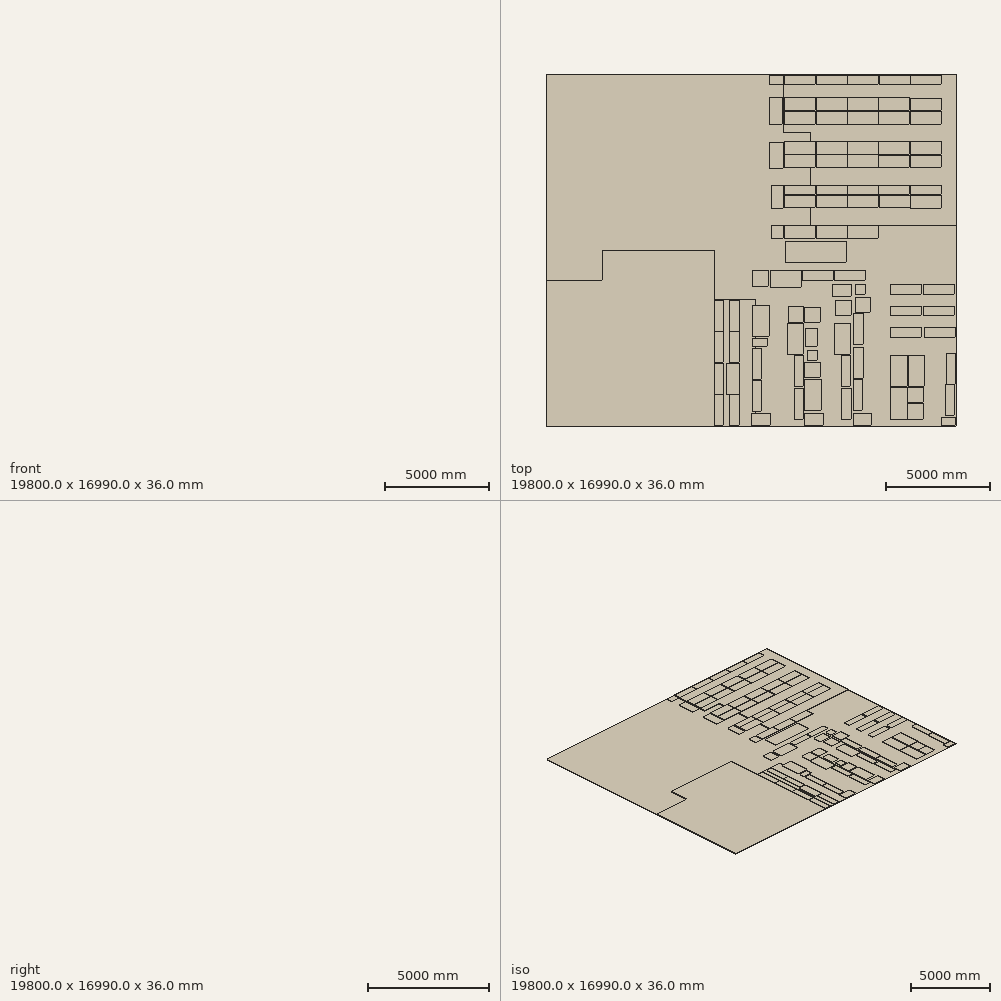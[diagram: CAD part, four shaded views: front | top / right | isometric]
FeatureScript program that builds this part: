
annotation { "Feature Type Name" : "Feature", "Feature Type Description" : "" }
export const myFeature = defineFeature(function(context is Context, id is Id, definition is map)
    precondition{}
    {
        {
            var Q0;
            Q0=qCreatedBy(makeId("Top.planeOp"),FACE);
            var sketch = newSketch(context, id + "F0", { "sketchPlane" : qUnion([Q0])});
            skLineSegment(sketch, "E0.bottom", {"start": v(9900, -8495) * mm, "end": v(-9900, -8495) * mm});
            skLineSegment(sketch, "E0.top", {"start": v(9900, 8495) * mm, "end": v(-9900, 8495) * mm});
            skLineSegment(sketch, "E0.left", {"start": v(9900, -8495) * mm, "end": v(9900, 8495) * mm});
            skLineSegment(sketch, "E0.right", {"start": v(-9900, -8495) * mm, "end": v(-9900, 8495) * mm});
            skPoint(sketch, "E0.middle", {"position": v(0, 0) * mm});
            skSolve(sketch);
        }
        {
            var Q0;
            Q0=qSketchRegion(id+"F0",true);
            extrude(context, id + "F1", {"entities" : qUnion([Q0]), "depth" : 10 * mm});
        }
        {
            var Q0;
            Q0=makeQuery(id+"F1.opExtrude","CAP_FACE",FACE,{"disambiguationData":[OSD([sQuery(id+"F0.wireOp",EDGE,"E0.bottom"),sQuery(id+"F0.wireOp",EDGE,"E0.top"),sQuery(id+"F0.wireOp",EDGE,"E0.left"),sQuery(id+"F0.wireOp",EDGE,"E0.right")])],"isStart":false});
            var sketch = newSketch(context, id + "F2", { "sketchPlane" : qUnion([Q0])});
            skLineSegment(sketch, "E1", {"start": v(-9900, -8495) * mm, "end": v(-9900, -1435) * mm});
            skLineSegment(sketch, "E2", {"start": v(-9900, -1435) * mm, "end": v(-7200, -1435) * mm});
            skLineSegment(sketch, "E3", {"start": v(-7200, -1435) * mm, "end": v(-7200, -5) * mm});
            skLineSegment(sketch, "E4", {"start": v(-7200, -5) * mm, "end": v(-1800, -5) * mm});
            skLineSegment(sketch, "E5", {"start": v(-1800, -5) * mm, "end": v(-1800, -2355) * mm});
            skLineSegment(sketch, "E6", {"start": v(-1800, -2355) * mm, "end": v(200, -2355) * mm});
            skLineSegment(sketch, "E7", {"start": v(200, -2355) * mm, "end": v(200, -8495) * mm});
            skLineSegment(sketch, "E8", {"start": v(200, -8495) * mm, "end": v(-9900, -8495) * mm});
            skLineSegment(sketch, "E9", {"start": v(9900, 1195) * mm, "end": v(9900, 8495) * mm});
            skLineSegment(sketch, "E10", {"start": v(9900, 8495) * mm, "end": v(1550, 8495) * mm});
            skLineSegment(sketch, "E11", {"start": v(1550, 8495) * mm, "end": v(1550, 5715) * mm});
            skLineSegment(sketch, "E12", {"start": v(1550, 5715) * mm, "end": v(2850, 5715) * mm});
            skLineSegment(sketch, "E13", {"start": v(2850, 5715) * mm, "end": v(2850, 1195) * mm});
            skLineSegment(sketch, "E14", {"start": v(2850, 1195) * mm, "end": v(9900, 1195) * mm});
            skLineSegment(sketch, "E15.left", {"start": v(3458.32, 469.72) * mm, "end": v(3008.32, 469.72) * mm});
            skPoint(sketch, "E15.middle", {"position": v(3233.32, -280.28) * mm});
            skLineSegment(sketch, "E16.left", {"start": v(4716.05, -36.44) * mm, "end": v(4096.05, -36.44) * mm});
            skPoint(sketch, "E16.middle", {"position": v(4406.05, -786.44) * mm});
            skSolve(sketch);
        }
        {
            var Q0;
            Q0=qSketchRegion(id+"F2",true);
            extrude(context, id + "F3", {"entities" : qUnion([Q0]), "operationType" : NewBodyOperationType.ADD, "depth" : 25 * mm});
        }
        {
            var Q0;
            Q0=makeQuery(id+"F3.opExtrude","CAP_FACE",FACE,{"disambiguationData":[OSD([sQuery(id+"F2.wireOp",EDGE,"E1"),sQuery(id+"F2.wireOp",EDGE,"E2"),sQuery(id+"F2.wireOp",EDGE,"E3"),sQuery(id+"F2.wireOp",EDGE,"E4"),sQuery(id+"F2.wireOp",EDGE,"E5"),sQuery(id+"F2.wireOp",EDGE,"E6"),sQuery(id+"F2.wireOp",EDGE,"E7"),sQuery(id+"F2.wireOp",EDGE,"E8")])],"isStart":false});
            var sketch = newSketch(context, id + "F4", { "sketchPlane" : qUnion([Q0])});
            skLineSegment(sketch, "E17.bottom", {"start": v(-1800, -8456.4) * mm, "end": v(-1800, -6956.4) * mm});
            skLineSegment(sketch, "E17.top", {"start": v(-1350, -8456.4) * mm, "end": v(-1350, -6956.4) * mm});
            skLineSegment(sketch, "E17.left", {"start": v(-1800, -8456.4) * mm, "end": v(-1350, -8456.4) * mm});
            skLineSegment(sketch, "E17.right", {"start": v(-1800, -6956.4) * mm, "end": v(-1350, -6956.4) * mm});
            skPoint(sketch, "E17.middle", {"position": v(-1575, -7706.4) * mm});
            skLineSegment(sketch, "E18.bottom", {"start": v(-1800, -6937.55) * mm, "end": v(-1800, -5437.55) * mm});
            skLineSegment(sketch, "E18.top", {"start": v(-1350, -6937.55) * mm, "end": v(-1350, -5437.55) * mm});
            skLineSegment(sketch, "E18.left", {"start": v(-1800, -6937.55) * mm, "end": v(-1350, -6937.55) * mm});
            skLineSegment(sketch, "E18.right", {"start": v(-1800, -5437.55) * mm, "end": v(-1350, -5437.55) * mm});
            skPoint(sketch, "E18.middle", {"position": v(-1575, -6187.55) * mm});
            skLineSegment(sketch, "E19.bottom", {"start": v(-1800, -5429.97) * mm, "end": v(-1800, -3929.97) * mm});
            skLineSegment(sketch, "E19.top", {"start": v(-1350, -5429.97) * mm, "end": v(-1350, -3929.97) * mm});
            skLineSegment(sketch, "E19.left", {"start": v(-1800, -5429.97) * mm, "end": v(-1350, -5429.97) * mm});
            skLineSegment(sketch, "E19.right", {"start": v(-1800, -3929.97) * mm, "end": v(-1350, -3929.97) * mm});
            skPoint(sketch, "E19.middle", {"position": v(-1575, -4679.97) * mm});
            skLineSegment(sketch, "E20.bottom", {"start": v(-1800, -3917.11) * mm, "end": v(-1800, -2417.11) * mm});
            skLineSegment(sketch, "E20.top", {"start": v(-1350, -3917.11) * mm, "end": v(-1350, -2417.11) * mm});
            skLineSegment(sketch, "E20.left", {"start": v(-1800, -3917.11) * mm, "end": v(-1350, -3917.11) * mm});
            skLineSegment(sketch, "E20.right", {"start": v(-1800, -2417.11) * mm, "end": v(-1350, -2417.11) * mm});
            skPoint(sketch, "E20.middle", {"position": v(-1575, -3167.11) * mm});
            skLineSegment(sketch, "E21.bottom", {"start": v(-1041.99, -8456.4) * mm, "end": v(-1041.99, -6956.4) * mm});
            skLineSegment(sketch, "E21.top", {"start": v(-591.99, -8456.4) * mm, "end": v(-591.99, -6956.4) * mm});
            skLineSegment(sketch, "E21.left", {"start": v(-1041.99, -8456.4) * mm, "end": v(-591.99, -8456.4) * mm});
            skLineSegment(sketch, "E21.right", {"start": v(-1041.99, -6956.4) * mm, "end": v(-591.99, -6956.4) * mm});
            skPoint(sketch, "E21.middle", {"position": v(-816.99, -7706.4) * mm});
            skLineSegment(sketch, "E22.bottom", {"start": v(-1210.98, -6937.55) * mm, "end": v(-1210.98, -5437.55) * mm});
            skLineSegment(sketch, "E22.top", {"start": v(-590.98, -6937.55) * mm, "end": v(-590.98, -5437.55) * mm});
            skLineSegment(sketch, "E22.left", {"start": v(-1210.98, -6937.55) * mm, "end": v(-590.98, -6937.55) * mm});
            skPoint(sketch, "E22.middle", {"position": v(-900.98, -6187.55) * mm});
            skLineSegment(sketch, "E23", {"start": v(-1210.98, -5437.55) * mm, "end": v(-590.98, -5437.55) * mm});
            skLineSegment(sketch, "E24.right", {"start": v(-1041.99, -5429.97) * mm, "end": v(-591.99, -5429.97) * mm});
            skLineSegment(sketch, "E25.bottom", {"start": v(-1041.99, -5422.4) * mm, "end": v(-1041.99, -3922.4) * mm});
            skLineSegment(sketch, "E25.top", {"start": v(-591.99, -5422.4) * mm, "end": v(-591.99, -3922.4) * mm});
            skLineSegment(sketch, "E25.left", {"start": v(-1041.99, -5422.4) * mm, "end": v(-591.99, -5422.4) * mm});
            skLineSegment(sketch, "E25.right", {"start": v(-1041.99, -3922.4) * mm, "end": v(-591.99, -3922.4) * mm});
            skPoint(sketch, "E25.middle", {"position": v(-816.99, -4672.4) * mm});
            skLineSegment(sketch, "E26.bottom", {"start": v(-1041.99, -3909.54) * mm, "end": v(-1041.99, -2409.54) * mm});
            skLineSegment(sketch, "E26.top", {"start": v(-591.99, -3909.54) * mm, "end": v(-591.99, -2409.54) * mm});
            skLineSegment(sketch, "E26.left", {"start": v(-1041.99, -3909.54) * mm, "end": v(-591.99, -3909.54) * mm});
            skLineSegment(sketch, "E26.right", {"start": v(-1041.99, -2409.54) * mm, "end": v(-591.99, -2409.54) * mm});
            skPoint(sketch, "E26.middle", {"position": v(-816.99, -3159.54) * mm});
            skLineSegment(sketch, "E27.bottom", {"start": v(1612.44, 5260.3) * mm, "end": v(3112.44, 5260.3) * mm});
            skLineSegment(sketch, "E27.top", {"start": v(1612.44, 4640.3) * mm, "end": v(3112.44, 4640.3) * mm});
            skLineSegment(sketch, "E27.left", {"start": v(1612.44, 5260.3) * mm, "end": v(1612.44, 4640.3) * mm});
            skPoint(sketch, "E27.middle", {"position": v(2799.14, 4542.43) * mm});
            skLineSegment(sketch, "E28", {"start": v(3112.44, 5260.3) * mm, "end": v(3112.44, 4640.3) * mm});
            skPoint(sketch, "E29.middle", {"position": v(6893.15, 886.64) * mm});
            skLineSegment(sketch, "E30.bottom", {"start": v(6135.57, 583.8) * mm, "end": v(4635.57, 583.8) * mm});
            skLineSegment(sketch, "E30.top", {"start": v(6135.57, 1203.8) * mm, "end": v(4635.57, 1203.8) * mm});
            skLineSegment(sketch, "E30.left", {"start": v(6135.57, 583.8) * mm, "end": v(6135.57, 1203.8) * mm});
            skLineSegment(sketch, "E30.right", {"start": v(4635.57, 583.8) * mm, "end": v(4635.57, 1203.8) * mm});
            skPoint(sketch, "E30.middle", {"position": v(5385.57, 893.8) * mm});
            skLineSegment(sketch, "E31.bottom", {"start": v(4622.71, 583.8) * mm, "end": v(3122.71, 583.8) * mm});
            skLineSegment(sketch, "E31.top", {"start": v(4622.71, 1203.8) * mm, "end": v(3122.71, 1203.8) * mm});
            skLineSegment(sketch, "E31.left", {"start": v(4622.71, 583.8) * mm, "end": v(4622.71, 1203.8) * mm});
            skLineSegment(sketch, "E31.right", {"start": v(3122.71, 583.8) * mm, "end": v(3122.71, 1203.8) * mm});
            skPoint(sketch, "E31.middle", {"position": v(3872.71, 893.8) * mm});
            skLineSegment(sketch, "E32.bottom", {"start": v(3112.44, 583.8) * mm, "end": v(1612.44, 583.8) * mm});
            skLineSegment(sketch, "E32.top", {"start": v(3112.44, 1203.8) * mm, "end": v(1612.44, 1203.8) * mm});
            skLineSegment(sketch, "E32.left", {"start": v(3112.44, 583.8) * mm, "end": v(3112.44, 1203.8) * mm});
            skLineSegment(sketch, "E32.right", {"start": v(1612.44, 583.8) * mm, "end": v(1612.44, 1203.8) * mm});
            skPoint(sketch, "E32.middle", {"position": v(2362.44, 893.8) * mm});
            skLineSegment(sketch, "E33.bottom", {"start": v(9167.32, 2047.04) * mm, "end": v(7667.32, 2047.04) * mm});
            skLineSegment(sketch, "E33.top", {"start": v(9167.32, 2667.04) * mm, "end": v(7667.32, 2667.04) * mm});
            skLineSegment(sketch, "E33.left", {"start": v(9167.32, 2047.04) * mm, "end": v(9167.32, 2667.04) * mm});
            skLineSegment(sketch, "E33.right", {"start": v(7667.32, 2047.04) * mm, "end": v(7667.32, 2667.04) * mm});
            skPoint(sketch, "E33.middle", {"position": v(8417.32, 2357.04) * mm});
            skLineSegment(sketch, "E34.bottom", {"start": v(7659.75, 2054.2) * mm, "end": v(6159.75, 2054.2) * mm});
            skLineSegment(sketch, "E34.top", {"start": v(7659.75, 2674.2) * mm, "end": v(6159.75, 2674.2) * mm});
            skLineSegment(sketch, "E34.left", {"start": v(7659.75, 2054.2) * mm, "end": v(7659.75, 2674.2) * mm});
            skLineSegment(sketch, "E34.right", {"start": v(6159.75, 2054.2) * mm, "end": v(6159.75, 2674.2) * mm});
            skPoint(sketch, "E34.middle", {"position": v(6909.75, 2364.2) * mm});
            skLineSegment(sketch, "E35.bottom", {"start": v(6146.89, 2054.2) * mm, "end": v(4646.89, 2054.2) * mm});
            skLineSegment(sketch, "E35.top", {"start": v(6146.89, 2674.2) * mm, "end": v(4646.89, 2674.2) * mm});
            skLineSegment(sketch, "E35.left", {"start": v(6146.89, 2054.2) * mm, "end": v(6146.89, 2674.2) * mm});
            skLineSegment(sketch, "E35.right", {"start": v(4646.89, 2054.2) * mm, "end": v(4646.89, 2674.2) * mm});
            skPoint(sketch, "E35.middle", {"position": v(5396.89, 2364.2) * mm});
            skLineSegment(sketch, "E36.bottom", {"start": v(4636.61, 2054.2) * mm, "end": v(3136.61, 2054.2) * mm});
            skLineSegment(sketch, "E36.top", {"start": v(4636.61, 2674.2) * mm, "end": v(3136.61, 2674.2) * mm});
            skLineSegment(sketch, "E36.left", {"start": v(4636.61, 2054.2) * mm, "end": v(4636.61, 2674.2) * mm});
            skLineSegment(sketch, "E36.right", {"start": v(3136.61, 2054.2) * mm, "end": v(3136.61, 2674.2) * mm});
            skPoint(sketch, "E36.middle", {"position": v(3886.61, 2364.2) * mm});
            skLineSegment(sketch, "E37.bottom", {"start": v(9167.32, 2686.65) * mm, "end": v(7667.32, 2686.65) * mm});
            skLineSegment(sketch, "E37.top", {"start": v(9167.32, 3136.65) * mm, "end": v(7667.32, 3136.65) * mm});
            skLineSegment(sketch, "E37.left", {"start": v(9167.32, 2686.65) * mm, "end": v(9167.32, 3136.65) * mm});
            skLineSegment(sketch, "E37.right", {"start": v(7667.32, 2686.65) * mm, "end": v(7667.32, 3136.65) * mm});
            skPoint(sketch, "E37.middle", {"position": v(8417.32, 2911.65) * mm});
            skLineSegment(sketch, "E38.bottom", {"start": v(7648.48, 2686.65) * mm, "end": v(6148.48, 2686.65) * mm});
            skLineSegment(sketch, "E38.top", {"start": v(7648.48, 3136.65) * mm, "end": v(6148.48, 3136.65) * mm});
            skLineSegment(sketch, "E38.left", {"start": v(7648.48, 2686.65) * mm, "end": v(7648.48, 3136.65) * mm});
            skLineSegment(sketch, "E38.right", {"start": v(6148.48, 2686.65) * mm, "end": v(6148.48, 3136.65) * mm});
            skPoint(sketch, "E38.middle", {"position": v(6898.48, 2911.65) * mm});
            skLineSegment(sketch, "E39.bottom", {"start": v(6137, 2686.65) * mm, "end": v(4637, 2686.65) * mm});
            skLineSegment(sketch, "E39.top", {"start": v(6137, 3136.65) * mm, "end": v(4637, 3136.65) * mm});
            skLineSegment(sketch, "E39.left", {"start": v(6137, 2686.65) * mm, "end": v(6137, 3136.65) * mm});
            skLineSegment(sketch, "E39.right", {"start": v(4637, 2686.65) * mm, "end": v(4637, 3136.65) * mm});
            skPoint(sketch, "E39.middle", {"position": v(5387, 2911.65) * mm});
            skLineSegment(sketch, "E40.bottom", {"start": v(4627.5, 2686.65) * mm, "end": v(3127.5, 2686.65) * mm});
            skLineSegment(sketch, "E40.top", {"start": v(4627.5, 3136.65) * mm, "end": v(3127.5, 3136.65) * mm});
            skLineSegment(sketch, "E40.left", {"start": v(4627.5, 2686.65) * mm, "end": v(4627.5, 3136.65) * mm});
            skLineSegment(sketch, "E40.right", {"start": v(3127.5, 2686.65) * mm, "end": v(3127.5, 3136.65) * mm});
            skPoint(sketch, "E40.middle", {"position": v(3877.5, 2911.65) * mm});
            skLineSegment(sketch, "E41.bottom", {"start": v(9167.32, 3986.65) * mm, "end": v(7667.32, 3986.65) * mm});
            skLineSegment(sketch, "E41.top", {"start": v(9167.32, 4606.65) * mm, "end": v(7667.32, 4606.65) * mm});
            skLineSegment(sketch, "E41.left", {"start": v(9167.32, 3986.65) * mm, "end": v(9167.32, 4606.65) * mm});
            skLineSegment(sketch, "E41.right", {"start": v(7667.32, 3986.65) * mm, "end": v(7667.32, 4606.65) * mm});
            skPoint(sketch, "E41.middle", {"position": v(8417.32, 4296.65) * mm});
            skLineSegment(sketch, "E42.bottom", {"start": v(7648.48, 3986.65) * mm, "end": v(6148.48, 3986.65) * mm});
            skLineSegment(sketch, "E42.top", {"start": v(7648.48, 4606.65) * mm, "end": v(6148.48, 4606.65) * mm});
            skLineSegment(sketch, "E42.left", {"start": v(7648.48, 3986.65) * mm, "end": v(7648.48, 4606.65) * mm});
            skLineSegment(sketch, "E42.right", {"start": v(6148.48, 3986.65) * mm, "end": v(6148.48, 4606.65) * mm});
            skPoint(sketch, "E42.middle", {"position": v(6898.48, 4296.65) * mm});
            skLineSegment(sketch, "E43.bottom", {"start": v(6140.9, 3993.8) * mm, "end": v(4640.9, 3993.8) * mm});
            skLineSegment(sketch, "E43.top", {"start": v(6140.9, 4613.8) * mm, "end": v(4640.9, 4613.8) * mm});
            skLineSegment(sketch, "E43.left", {"start": v(6140.9, 3993.8) * mm, "end": v(6140.9, 4613.8) * mm});
            skLineSegment(sketch, "E43.right", {"start": v(4640.9, 3993.8) * mm, "end": v(4640.9, 4613.8) * mm});
            skPoint(sketch, "E43.middle", {"position": v(5390.9, 4303.8) * mm});
            skLineSegment(sketch, "E44.bottom", {"start": v(4628.05, 3993.8) * mm, "end": v(3128.05, 3993.8) * mm});
            skLineSegment(sketch, "E44.top", {"start": v(4628.05, 4613.8) * mm, "end": v(3128.05, 4613.8) * mm});
            skLineSegment(sketch, "E44.left", {"start": v(4628.05, 3993.8) * mm, "end": v(4628.05, 4613.8) * mm});
            skLineSegment(sketch, "E44.right", {"start": v(3128.05, 3993.8) * mm, "end": v(3128.05, 4613.8) * mm});
            skPoint(sketch, "E44.middle", {"position": v(3878.05, 4303.8) * mm});
            skLineSegment(sketch, "E45.bottom", {"start": v(9155.83, 4632.29) * mm, "end": v(7655.83, 4632.29) * mm});
            skLineSegment(sketch, "E45.top", {"start": v(9155.83, 5252.29) * mm, "end": v(7655.83, 5252.29) * mm});
            skLineSegment(sketch, "E45.left", {"start": v(9155.83, 4632.29) * mm, "end": v(9155.83, 5252.29) * mm});
            skLineSegment(sketch, "E45.right", {"start": v(7655.83, 4632.29) * mm, "end": v(7655.83, 5252.29) * mm});
            skPoint(sketch, "E45.middle", {"position": v(8405.83, 4942.29) * mm});
            skLineSegment(sketch, "E46.bottom", {"start": v(7636.99, 4632.29) * mm, "end": v(6136.99, 4632.29) * mm});
            skLineSegment(sketch, "E46.top", {"start": v(7636.99, 5252.29) * mm, "end": v(6136.99, 5252.29) * mm});
            skLineSegment(sketch, "E46.left", {"start": v(7636.99, 4632.29) * mm, "end": v(7636.99, 5252.29) * mm});
            skLineSegment(sketch, "E46.right", {"start": v(6136.99, 4632.29) * mm, "end": v(6136.99, 5252.29) * mm});
            skPoint(sketch, "E46.middle", {"position": v(6886.99, 4942.29) * mm});
            skLineSegment(sketch, "E47.bottom", {"start": v(6129.41, 4639.45) * mm, "end": v(4629.41, 4639.45) * mm});
            skLineSegment(sketch, "E47.top", {"start": v(6129.41, 5259.45) * mm, "end": v(4629.41, 5259.45) * mm});
            skLineSegment(sketch, "E47.left", {"start": v(6129.41, 4639.45) * mm, "end": v(6129.41, 5259.45) * mm});
            skLineSegment(sketch, "E47.right", {"start": v(4629.41, 4639.45) * mm, "end": v(4629.41, 5259.45) * mm});
            skPoint(sketch, "E47.middle", {"position": v(5379.41, 4949.45) * mm});
            skLineSegment(sketch, "E48.bottom", {"start": v(4616.55, 4639.45) * mm, "end": v(3116.55, 4639.45) * mm});
            skLineSegment(sketch, "E48.top", {"start": v(4616.55, 5259.45) * mm, "end": v(3116.55, 5259.45) * mm});
            skLineSegment(sketch, "E48.left", {"start": v(4616.55, 4639.45) * mm, "end": v(4616.55, 5259.45) * mm});
            skLineSegment(sketch, "E48.right", {"start": v(3116.55, 4639.45) * mm, "end": v(3116.55, 5259.45) * mm});
            skPoint(sketch, "E48.middle", {"position": v(3866.55, 4949.45) * mm});
            skLineSegment(sketch, "E49.bottom", {"start": v(9155.83, 6094.59) * mm, "end": v(7655.83, 6094.59) * mm});
            skLineSegment(sketch, "E49.top", {"start": v(9155.83, 6714.59) * mm, "end": v(7655.83, 6714.59) * mm});
            skLineSegment(sketch, "E49.left", {"start": v(9155.83, 6094.59) * mm, "end": v(9155.83, 6714.59) * mm});
            skLineSegment(sketch, "E49.right", {"start": v(7655.83, 6094.59) * mm, "end": v(7655.83, 6714.59) * mm});
            skPoint(sketch, "E49.middle", {"position": v(8405.83, 6404.59) * mm});
            skLineSegment(sketch, "E50.bottom", {"start": v(7636.99, 6098.15) * mm, "end": v(6136.99, 6098.15) * mm});
            skLineSegment(sketch, "E50.top", {"start": v(7636.99, 6718.15) * mm, "end": v(6136.99, 6718.15) * mm});
            skLineSegment(sketch, "E50.left", {"start": v(7636.99, 6098.15) * mm, "end": v(7636.99, 6718.15) * mm});
            skLineSegment(sketch, "E50.right", {"start": v(6136.99, 6098.15) * mm, "end": v(6136.99, 6718.15) * mm});
            skPoint(sketch, "E50.middle", {"position": v(6886.99, 6408.15) * mm});
            skLineSegment(sketch, "E51.bottom", {"start": v(6129.41, 6105.31) * mm, "end": v(4629.41, 6105.31) * mm});
            skLineSegment(sketch, "E51.top", {"start": v(6129.41, 6725.31) * mm, "end": v(4629.41, 6725.31) * mm});
            skLineSegment(sketch, "E51.left", {"start": v(6129.41, 6105.31) * mm, "end": v(6129.41, 6725.31) * mm});
            skLineSegment(sketch, "E51.right", {"start": v(4629.41, 6105.31) * mm, "end": v(4629.41, 6725.31) * mm});
            skPoint(sketch, "E51.middle", {"position": v(5379.41, 6415.31) * mm});
            skLineSegment(sketch, "E52.bottom", {"start": v(4616.55, 6105.31) * mm, "end": v(3116.55, 6105.31) * mm});
            skLineSegment(sketch, "E52.top", {"start": v(4616.55, 6725.31) * mm, "end": v(3116.55, 6725.31) * mm});
            skLineSegment(sketch, "E52.left", {"start": v(4616.55, 6105.31) * mm, "end": v(4616.55, 6725.31) * mm});
            skLineSegment(sketch, "E52.right", {"start": v(3116.55, 6105.31) * mm, "end": v(3116.55, 6725.31) * mm});
            skPoint(sketch, "E52.middle", {"position": v(3866.55, 6415.31) * mm});
            skLineSegment(sketch, "E53.bottom", {"start": v(3106.28, 6105.31) * mm, "end": v(1606.28, 6105.31) * mm});
            skLineSegment(sketch, "E53.top", {"start": v(3106.28, 6725.31) * mm, "end": v(1606.28, 6725.31) * mm});
            skLineSegment(sketch, "E53.left", {"start": v(3106.28, 6105.31) * mm, "end": v(3106.28, 6725.31) * mm});
            skLineSegment(sketch, "E53.right", {"start": v(1606.28, 6105.31) * mm, "end": v(1606.28, 6725.31) * mm});
            skPoint(sketch, "E53.middle", {"position": v(2356.28, 6415.31) * mm});
            skLineSegment(sketch, "E54.bottom", {"start": v(9156.24, 6741.08) * mm, "end": v(7656.24, 6741.08) * mm});
            skLineSegment(sketch, "E54.top", {"start": v(9156.24, 7361.08) * mm, "end": v(7656.24, 7361.08) * mm});
            skLineSegment(sketch, "E54.left", {"start": v(9156.24, 6741.08) * mm, "end": v(9156.24, 7361.08) * mm});
            skLineSegment(sketch, "E54.right", {"start": v(7656.24, 6741.08) * mm, "end": v(7656.24, 7361.08) * mm});
            skPoint(sketch, "E54.middle", {"position": v(8406.24, 7051.08) * mm});
            skPoint(sketch, "E55.middle", {"position": v(6887.4, 7054.64) * mm});
            skLineSegment(sketch, "E56.bottom", {"start": v(6129.82, 6751.8) * mm, "end": v(4629.82, 6751.8) * mm});
            skLineSegment(sketch, "E56.top", {"start": v(6129.82, 7371.8) * mm, "end": v(4629.82, 7371.8) * mm});
            skLineSegment(sketch, "E56.left", {"start": v(6129.82, 6751.8) * mm, "end": v(6129.82, 7371.8) * mm});
            skLineSegment(sketch, "E56.right", {"start": v(4629.82, 6751.8) * mm, "end": v(4629.82, 7371.8) * mm});
            skPoint(sketch, "E56.middle", {"position": v(5379.82, 7061.8) * mm});
            skLineSegment(sketch, "E57.bottom", {"start": v(4616.96, 6751.8) * mm, "end": v(3116.96, 6751.8) * mm});
            skLineSegment(sketch, "E57.top", {"start": v(4616.96, 7371.8) * mm, "end": v(3116.96, 7371.8) * mm});
            skLineSegment(sketch, "E57.left", {"start": v(4616.96, 6751.8) * mm, "end": v(4616.96, 7371.8) * mm});
            skLineSegment(sketch, "E57.right", {"start": v(3116.96, 6751.8) * mm, "end": v(3116.96, 7371.8) * mm});
            skPoint(sketch, "E57.middle", {"position": v(3866.96, 7061.8) * mm});
            skLineSegment(sketch, "E58.bottom", {"start": v(3106.69, 6751.8) * mm, "end": v(1606.69, 6751.8) * mm});
            skLineSegment(sketch, "E58.top", {"start": v(3106.69, 7371.8) * mm, "end": v(1606.69, 7371.8) * mm});
            skLineSegment(sketch, "E58.left", {"start": v(3106.69, 6751.8) * mm, "end": v(3106.69, 7371.8) * mm});
            skLineSegment(sketch, "E58.right", {"start": v(1606.69, 6751.8) * mm, "end": v(1606.69, 7371.8) * mm});
            skPoint(sketch, "E58.middle", {"position": v(2356.69, 7061.8) * mm});
            skPoint(sketch, "E59.middle", {"position": v(6886.99, 7134.11) * mm});
            skLineSegment(sketch, "E60.bottom", {"start": v(1612.44, 4613.8) * mm, "end": v(3112.44, 4613.8) * mm});
            skLineSegment(sketch, "E60.top", {"start": v(1612.44, 3993.8) * mm, "end": v(3112.44, 3993.8) * mm});
            skLineSegment(sketch, "E60.left", {"start": v(1612.44, 4613.8) * mm, "end": v(1612.44, 3993.8) * mm});
            skLineSegment(sketch, "E61", {"start": v(3112.44, 4613.8) * mm, "end": v(3112.44, 3993.8) * mm});
            skLineSegment(sketch, "E62.bottom", {"start": v(1612.44, 3136.65) * mm, "end": v(3112.44, 3136.65) * mm});
            skLineSegment(sketch, "E62.top", {"start": v(1612.44, 2686.65) * mm, "end": v(3112.44, 2686.65) * mm});
            skLineSegment(sketch, "E62.left", {"start": v(1612.44, 3136.65) * mm, "end": v(1612.44, 2686.65) * mm});
            skLineSegment(sketch, "E62.right", {"start": v(3112.44, 3136.65) * mm, "end": v(3112.44, 2686.65) * mm});
            skLineSegment(sketch, "E63.bottom", {"start": v(1612.44, 8467.65) * mm, "end": v(3112.44, 8467.65) * mm});
            skLineSegment(sketch, "E63.top", {"start": v(1612.44, 8017.65) * mm, "end": v(3112.44, 8017.65) * mm});
            skLineSegment(sketch, "E63.left", {"start": v(1612.44, 8467.65) * mm, "end": v(1612.44, 8017.65) * mm});
            skLineSegment(sketch, "E63.right", {"start": v(3112.44, 8467.65) * mm, "end": v(3112.44, 8017.65) * mm});
            skLineSegment(sketch, "E64.bottom", {"start": v(3136.61, 8467.65) * mm, "end": v(4636.61, 8467.65) * mm});
            skLineSegment(sketch, "E64.top", {"start": v(3136.61, 8017.65) * mm, "end": v(4636.61, 8017.65) * mm});
            skLineSegment(sketch, "E64.left", {"start": v(3136.61, 8467.65) * mm, "end": v(3136.61, 8017.65) * mm});
            skLineSegment(sketch, "E64.right", {"start": v(4636.61, 8467.65) * mm, "end": v(4636.61, 8017.65) * mm});
            skLineSegment(sketch, "E65.bottom", {"start": v(4646.89, 8467.65) * mm, "end": v(6146.89, 8467.65) * mm});
            skLineSegment(sketch, "E65.top", {"start": v(4646.89, 8017.65) * mm, "end": v(6146.89, 8017.65) * mm});
            skLineSegment(sketch, "E65.left", {"start": v(4646.89, 8467.65) * mm, "end": v(4646.89, 8017.65) * mm});
            skLineSegment(sketch, "E65.right", {"start": v(6146.89, 8467.65) * mm, "end": v(6146.89, 8017.65) * mm});
            skLineSegment(sketch, "E66.bottom", {"start": v(6186.86, 8467.65) * mm, "end": v(7686.86, 8467.65) * mm});
            skLineSegment(sketch, "E66.top", {"start": v(6186.86, 8017.65) * mm, "end": v(7686.86, 8017.65) * mm});
            skLineSegment(sketch, "E66.left", {"start": v(6186.86, 8467.65) * mm, "end": v(6186.86, 8017.65) * mm});
            skLineSegment(sketch, "E66.right", {"start": v(7686.86, 8467.65) * mm, "end": v(7686.86, 8017.65) * mm});
            skLineSegment(sketch, "E67.bottom", {"start": v(7694.44, 8467.65) * mm, "end": v(9194.44, 8467.65) * mm});
            skLineSegment(sketch, "E67.top", {"start": v(7694.44, 8017.65) * mm, "end": v(9194.44, 8017.65) * mm});
            skLineSegment(sketch, "E67.left", {"start": v(7694.44, 8467.65) * mm, "end": v(7694.44, 8017.65) * mm});
            skLineSegment(sketch, "E67.right", {"start": v(9194.44, 8467.65) * mm, "end": v(9194.44, 8017.65) * mm});
            skLineSegment(sketch, "E68.top", {"start": v(7648.48, 7371.8) * mm, "end": v(6148.48, 7371.8) * mm});
            skLineSegment(sketch, "E68.left", {"start": v(7648.48, 6751.8) * mm, "end": v(7648.48, 7371.8) * mm});
            skLineSegment(sketch, "E68.right", {"start": v(6148.48, 6751.8) * mm, "end": v(6148.48, 7371.8) * mm});
            skLineSegment(sketch, "E69", {"start": v(6148.48, 6751.8) * mm, "end": v(7648.48, 6751.8) * mm});
            skPoint(sketch, "E70.middle", {"position": v(8422.9, 893.4) * mm});
            skLineSegment(sketch, "E71.bottom", {"start": v(3112.44, 2054.2) * mm, "end": v(1612.44, 2054.2) * mm});
            skLineSegment(sketch, "E71.top", {"start": v(3112.44, 2674.2) * mm, "end": v(1612.44, 2674.2) * mm});
            skLineSegment(sketch, "E71.left", {"start": v(3112.44, 2054.2) * mm, "end": v(3112.44, 2674.2) * mm});
            skLineSegment(sketch, "E71.right", {"start": v(1612.44, 2054.2) * mm, "end": v(1612.44, 2674.2) * mm});
            skLineSegment(sketch, "E72.bottom", {"start": v(883.45, 7368.6) * mm, "end": v(1505.1, 7368.6) * mm});
            skLineSegment(sketch, "E72.top", {"start": v(883.45, 6108.72) * mm, "end": v(1505.1, 6108.72) * mm});
            skLineSegment(sketch, "E72.left", {"start": v(883.45, 7368.6) * mm, "end": v(883.45, 6108.72) * mm});
            skLineSegment(sketch, "E72.right", {"start": v(1505.1, 7368.6) * mm, "end": v(1505.1, 6108.72) * mm});
            skLineSegment(sketch, "E73.bottom", {"start": v(883.45, 8459.2) * mm, "end": v(1536.28, 8459.2) * mm});
            skLineSegment(sketch, "E73.top", {"start": v(883.45, 8023.53) * mm, "end": v(1536.28, 8023.53) * mm});
            skLineSegment(sketch, "E73.left", {"start": v(883.45, 8459.2) * mm, "end": v(883.45, 8023.53) * mm});
            skLineSegment(sketch, "E73.right", {"start": v(1536.28, 8459.2) * mm, "end": v(1536.28, 8023.53) * mm});
            skLineSegment(sketch, "E74.bottom", {"start": v(883.45, 5224.85) * mm, "end": v(1536.28, 5224.85) * mm});
            skLineSegment(sketch, "E74.top", {"start": v(883.45, 3969.5) * mm, "end": v(1536.28, 3969.5) * mm});
            skLineSegment(sketch, "E74.left", {"start": v(883.45, 5224.85) * mm, "end": v(883.45, 3969.5) * mm});
            skLineSegment(sketch, "E74.right", {"start": v(1536.28, 5224.85) * mm, "end": v(1536.28, 3969.5) * mm});
            skLineSegment(sketch, "E75.bottom", {"start": v(952.91, 3120.3) * mm, "end": v(1521.51, 3120.3) * mm});
            skLineSegment(sketch, "E75.top", {"start": v(952.91, 2034.8) * mm, "end": v(1521.51, 2034.8) * mm});
            skLineSegment(sketch, "E75.left", {"start": v(952.91, 3120.3) * mm, "end": v(952.91, 2034.8) * mm});
            skLineSegment(sketch, "E75.right", {"start": v(1521.51, 3120.3) * mm, "end": v(1521.51, 2034.8) * mm});
            skLineSegment(sketch, "E76.bottom", {"start": v(945.53, 1207.76) * mm, "end": v(1536.28, 1207.76) * mm});
            skLineSegment(sketch, "E76.top", {"start": v(945.53, 580.08) * mm, "end": v(1536.28, 580.08) * mm});
            skLineSegment(sketch, "E76.left", {"start": v(945.53, 1207.76) * mm, "end": v(945.53, 580.08) * mm});
            skLineSegment(sketch, "E76.right", {"start": v(1536.28, 1207.76) * mm, "end": v(1536.28, 580.08) * mm});
            skLineSegment(sketch, "E77.bottom", {"start": v(1624.87, 424.62) * mm, "end": v(4608.15, 424.62) * mm});
            skLineSegment(sketch, "E77.top", {"start": v(1624.87, -575.38) * mm, "end": v(4608.15, -575.38) * mm});
            skLineSegment(sketch, "E77.left", {"start": v(1624.87, 424.62) * mm, "end": v(1624.87, -575.38) * mm});
            skLineSegment(sketch, "E77.right", {"start": v(4608.15, 424.62) * mm, "end": v(4608.15, -575.38) * mm});
            skLineSegment(sketch, "E78.bottom", {"start": v(5005.03, -2259.98) * mm, "end": v(5755.03, -2259.98) * mm});
            skLineSegment(sketch, "E78.top", {"start": v(5005.03, -3009.98) * mm, "end": v(5755.03, -3009.98) * mm});
            skLineSegment(sketch, "E78.left", {"start": v(5005.03, -2259.98) * mm, "end": v(5005.03, -3009.98) * mm});
            skLineSegment(sketch, "E78.right", {"start": v(5755.03, -2259.98) * mm, "end": v(5755.03, -3009.98) * mm});
            skLineSegment(sketch, "E79.bottom", {"start": v(10, -7856.4) * mm, "end": v(910, -7856.4) * mm});
            skLineSegment(sketch, "E79.top", {"start": v(10, -8456.4) * mm, "end": v(910, -8456.4) * mm});
            skLineSegment(sketch, "E79.left", {"start": v(10, -7856.4) * mm, "end": v(10, -8456.4) * mm});
            skLineSegment(sketch, "E79.right", {"start": v(910, -7856.4) * mm, "end": v(910, -8456.4) * mm});
            skLineSegment(sketch, "E80.bottom", {"start": v(56.53, -7786.4) * mm, "end": v(56.53, -6286.4) * mm});
            skLineSegment(sketch, "E80.top", {"start": v(506.53, -7786.4) * mm, "end": v(506.53, -6286.4) * mm});
            skLineSegment(sketch, "E80.left", {"start": v(56.53, -7786.4) * mm, "end": v(506.53, -7786.4) * mm});
            skLineSegment(sketch, "E80.right", {"start": v(56.53, -6286.4) * mm, "end": v(506.53, -6286.4) * mm});
            skLineSegment(sketch, "E81.bottom", {"start": v(56.53, -6237.55) * mm, "end": v(56.53, -4737.55) * mm});
            skLineSegment(sketch, "E81.top", {"start": v(506.53, -6237.55) * mm, "end": v(506.53, -4737.55) * mm});
            skLineSegment(sketch, "E81.left", {"start": v(56.53, -6237.55) * mm, "end": v(506.53, -6237.55) * mm});
            skLineSegment(sketch, "E81.right", {"start": v(56.53, -4737.55) * mm, "end": v(506.53, -4737.55) * mm});
            skLineSegment(sketch, "E82.bottom", {"start": v(56.53, -980.76) * mm, "end": v(806.53, -980.76) * mm});
            skLineSegment(sketch, "E82.top", {"start": v(56.53, -1730.76) * mm, "end": v(806.53, -1730.76) * mm});
            skLineSegment(sketch, "E82.left", {"start": v(56.53, -980.76) * mm, "end": v(56.53, -1730.76) * mm});
            skLineSegment(sketch, "E82.right", {"start": v(806.53, -980.76) * mm, "end": v(806.53, -1730.76) * mm});
            skLineSegment(sketch, "E83.bottom", {"start": v(2404.2, -980.76) * mm, "end": v(2404.2, -1780.76) * mm});
            skLineSegment(sketch, "E83.top", {"start": v(904.2, -980.76) * mm, "end": v(904.2, -1780.76) * mm});
            skLineSegment(sketch, "E83.left", {"start": v(2404.2, -980.76) * mm, "end": v(904.2, -980.76) * mm});
            skLineSegment(sketch, "E83.right", {"start": v(2404.2, -1780.76) * mm, "end": v(904.2, -1780.76) * mm});
            skLineSegment(sketch, "E84.bottom", {"start": v(2471.14, -980.76) * mm, "end": v(3971.14, -980.76) * mm});
            skLineSegment(sketch, "E84.top", {"start": v(2471.14, -1430.76) * mm, "end": v(3971.14, -1430.76) * mm});
            skLineSegment(sketch, "E84.left", {"start": v(2471.14, -980.76) * mm, "end": v(2471.14, -1430.76) * mm});
            skLineSegment(sketch, "E84.right", {"start": v(3971.14, -980.76) * mm, "end": v(3971.14, -1430.76) * mm});
            skLineSegment(sketch, "E85.bottom", {"start": v(4001.14, -980.76) * mm, "end": v(5501.14, -980.76) * mm});
            skLineSegment(sketch, "E85.top", {"start": v(4001.14, -1430.76) * mm, "end": v(5501.14, -1430.76) * mm});
            skLineSegment(sketch, "E85.left", {"start": v(4001.14, -980.76) * mm, "end": v(4001.14, -1430.76) * mm});
            skLineSegment(sketch, "E85.right", {"start": v(5501.14, -980.76) * mm, "end": v(5501.14, -1430.76) * mm});
            skLineSegment(sketch, "E86.bottom", {"start": v(1767.35, -2709.54) * mm, "end": v(2517.35, -2709.54) * mm});
            skLineSegment(sketch, "E86.top", {"start": v(1767.35, -3459.54) * mm, "end": v(2517.35, -3459.54) * mm});
            skLineSegment(sketch, "E86.left", {"start": v(1767.35, -2709.54) * mm, "end": v(1767.35, -3459.54) * mm});
            skLineSegment(sketch, "E86.right", {"start": v(2517.35, -2709.54) * mm, "end": v(2517.35, -3459.54) * mm});
            skLineSegment(sketch, "E87.bottom", {"start": v(1717.35, -3509.98) * mm, "end": v(2517.35, -3509.98) * mm});
            skLineSegment(sketch, "E87.top", {"start": v(1717.35, -5009.98) * mm, "end": v(2517.35, -5009.98) * mm});
            skLineSegment(sketch, "E87.left", {"start": v(1717.35, -3509.98) * mm, "end": v(1717.35, -5009.98) * mm});
            skLineSegment(sketch, "E87.right", {"start": v(2517.35, -3509.98) * mm, "end": v(2517.35, -5009.98) * mm});
            skLineSegment(sketch, "E88.bottom", {"start": v(2079.98, -8148.39) * mm, "end": v(2079.98, -6648.39) * mm});
            skLineSegment(sketch, "E88.top", {"start": v(2529.98, -8148.39) * mm, "end": v(2529.98, -6648.39) * mm});
            skLineSegment(sketch, "E88.left", {"start": v(2079.98, -8148.39) * mm, "end": v(2529.98, -8148.39) * mm});
            skLineSegment(sketch, "E88.right", {"start": v(2079.98, -6648.39) * mm, "end": v(2529.98, -6648.39) * mm});
            skLineSegment(sketch, "E89.bottom", {"start": v(2072.87, -6582.86) * mm, "end": v(2072.87, -5082.86) * mm});
            skLineSegment(sketch, "E89.top", {"start": v(2522.87, -6582.86) * mm, "end": v(2522.87, -5082.86) * mm});
            skLineSegment(sketch, "E89.left", {"start": v(2072.87, -6582.86) * mm, "end": v(2522.87, -6582.86) * mm});
            skLineSegment(sketch, "E89.right", {"start": v(2072.87, -5082.86) * mm, "end": v(2522.87, -5082.86) * mm});
            skLineSegment(sketch, "E90.bottom", {"start": v(2569.98, -7856.4) * mm, "end": v(3469.98, -7856.4) * mm});
            skLineSegment(sketch, "E90.top", {"start": v(2569.98, -8456.4) * mm, "end": v(3469.98, -8456.4) * mm});
            skLineSegment(sketch, "E90.left", {"start": v(2569.98, -7856.4) * mm, "end": v(2569.98, -8456.4) * mm});
            skLineSegment(sketch, "E90.right", {"start": v(3469.98, -7856.4) * mm, "end": v(3469.98, -8456.4) * mm});
            skLineSegment(sketch, "E91.bottom", {"start": v(2569.98, -5387.55) * mm, "end": v(3319.98, -5387.55) * mm});
            skLineSegment(sketch, "E91.top", {"start": v(2569.98, -6137.55) * mm, "end": v(3319.98, -6137.55) * mm});
            skLineSegment(sketch, "E91.left", {"start": v(2569.98, -5387.55) * mm, "end": v(2569.98, -6137.55) * mm});
            skLineSegment(sketch, "E91.right", {"start": v(3319.98, -5387.55) * mm, "end": v(3319.98, -6137.55) * mm});
            skLineSegment(sketch, "E92.bottom", {"start": v(5020.1, -1624.38) * mm, "end": v(5520.1, -1624.38) * mm});
            skLineSegment(sketch, "E92.top", {"start": v(5020.1, -2124.38) * mm, "end": v(5520.1, -2124.38) * mm});
            skLineSegment(sketch, "E92.left", {"start": v(5020.1, -1624.38) * mm, "end": v(5020.1, -2124.38) * mm});
            skLineSegment(sketch, "E92.right", {"start": v(5520.1, -1624.38) * mm, "end": v(5520.1, -2124.38) * mm});
            skLineSegment(sketch, "E93.bottom", {"start": v(2695.73, -4822.86) * mm, "end": v(3195.73, -4822.86) * mm});
            skLineSegment(sketch, "E93.top", {"start": v(2695.73, -5322.86) * mm, "end": v(3195.73, -5322.86) * mm});
            skLineSegment(sketch, "E93.left", {"start": v(2695.73, -4822.86) * mm, "end": v(2695.73, -5322.86) * mm});
            skLineSegment(sketch, "E93.right", {"start": v(3195.73, -4822.86) * mm, "end": v(3195.73, -5322.86) * mm});
            skLineSegment(sketch, "E94.bottom", {"start": v(2569.98, -2759.98) * mm, "end": v(3319.98, -2759.98) * mm});
            skLineSegment(sketch, "E94.top", {"start": v(2569.98, -3459.54) * mm, "end": v(3319.98, -3459.54) * mm});
            skLineSegment(sketch, "E94.left", {"start": v(2569.98, -2709.54) * mm, "end": v(2569.98, -3459.54) * mm});
            skLineSegment(sketch, "E94.right", {"start": v(3319.98, -2709.54) * mm, "end": v(3319.98, -3459.54) * mm});
            skLineSegment(sketch, "E95.bottom", {"start": v(2569.98, -6206.4) * mm, "end": v(3369.98, -6206.4) * mm});
            skLineSegment(sketch, "E95.top", {"start": v(2569.98, -7706.4) * mm, "end": v(3369.98, -7706.4) * mm});
            skLineSegment(sketch, "E95.left", {"start": v(2569.98, -6206.4) * mm, "end": v(2569.98, -7706.4) * mm});
            skLineSegment(sketch, "E95.right", {"start": v(3369.98, -6206.4) * mm, "end": v(3369.98, -7706.4) * mm});
            skLineSegment(sketch, "E96.bottom", {"start": v(3205.45, -3758.74) * mm, "end": v(3205.45, -4658.74) * mm});
            skLineSegment(sketch, "E96.top", {"start": v(2605.45, -3758.74) * mm, "end": v(2605.45, -4658.74) * mm});
            skLineSegment(sketch, "E96.left", {"start": v(3205.45, -3758.74) * mm, "end": v(2605.45, -3758.74) * mm});
            skLineSegment(sketch, "E96.right", {"start": v(3205.45, -4658.74) * mm, "end": v(2605.45, -4658.74) * mm});
            skLineSegment(sketch, "E97.bottom", {"start": v(3915.03, -1644.38) * mm, "end": v(4815.03, -1644.38) * mm});
            skLineSegment(sketch, "E97.top", {"start": v(3915.03, -2244.38) * mm, "end": v(4815.03, -2244.38) * mm});
            skLineSegment(sketch, "E97.left", {"start": v(3915.03, -1644.38) * mm, "end": v(3915.03, -2244.38) * mm});
            skLineSegment(sketch, "E97.right", {"start": v(4815.03, -1644.38) * mm, "end": v(4815.03, -2244.38) * mm});
            skLineSegment(sketch, "E98.bottom", {"start": v(4079.25, -2409.54) * mm, "end": v(4829.25, -2409.54) * mm});
            skLineSegment(sketch, "E98.top", {"start": v(4079.25, -3159.54) * mm, "end": v(4829.25, -3159.54) * mm});
            skLineSegment(sketch, "E98.left", {"start": v(4079.25, -2409.54) * mm, "end": v(4079.25, -3159.54) * mm});
            skLineSegment(sketch, "E98.right", {"start": v(4829.25, -2409.54) * mm, "end": v(4829.25, -3159.54) * mm});
            skLineSegment(sketch, "E99.bottom", {"start": v(4001.25, -3509.98) * mm, "end": v(4801.25, -3509.98) * mm});
            skLineSegment(sketch, "E99.top", {"start": v(4001.25, -5009.98) * mm, "end": v(4801.25, -5009.98) * mm});
            skLineSegment(sketch, "E99.left", {"start": v(4001.25, -3509.98) * mm, "end": v(4001.25, -5009.98) * mm});
            skLineSegment(sketch, "E99.right", {"start": v(4801.25, -3509.98) * mm, "end": v(4801.25, -5009.98) * mm});
            skLineSegment(sketch, "E100.bottom", {"start": v(4360.02, -8148.39) * mm, "end": v(4360.02, -6648.39) * mm});
            skLineSegment(sketch, "E100.top", {"start": v(4810.02, -8148.39) * mm, "end": v(4810.02, -6648.39) * mm});
            skLineSegment(sketch, "E100.left", {"start": v(4360.02, -8148.39) * mm, "end": v(4810.02, -8148.39) * mm});
            skLineSegment(sketch, "E100.right", {"start": v(4360.02, -6648.39) * mm, "end": v(4810.02, -6648.39) * mm});
            skLineSegment(sketch, "E101.bottom", {"start": v(4336.8, -6564.93) * mm, "end": v(4336.8, -5064.93) * mm});
            skLineSegment(sketch, "E101.top", {"start": v(4786.8, -6564.93) * mm, "end": v(4786.8, -5064.93) * mm});
            skLineSegment(sketch, "E101.left", {"start": v(4336.8, -6564.93) * mm, "end": v(4786.8, -6564.93) * mm});
            skLineSegment(sketch, "E101.right", {"start": v(4336.8, -5064.93) * mm, "end": v(4786.8, -5064.93) * mm});
            skLineSegment(sketch, "E102.bottom", {"start": v(4934.69, -4559.5) * mm, "end": v(4934.69, -3059.5) * mm});
            skLineSegment(sketch, "E102.top", {"start": v(5384.69, -4559.5) * mm, "end": v(5384.69, -3059.5) * mm});
            skLineSegment(sketch, "E102.left", {"start": v(4934.69, -4559.5) * mm, "end": v(5384.69, -4559.5) * mm});
            skLineSegment(sketch, "E102.right", {"start": v(4934.69, -3059.5) * mm, "end": v(5384.69, -3059.5) * mm});
            skLineSegment(sketch, "E103.bottom", {"start": v(4934.69, -6199.04) * mm, "end": v(4934.69, -4699.04) * mm});
            skLineSegment(sketch, "E103.top", {"start": v(5384.69, -6199.04) * mm, "end": v(5384.69, -4699.04) * mm});
            skLineSegment(sketch, "E103.left", {"start": v(4934.69, -6199.04) * mm, "end": v(5384.69, -6199.04) * mm});
            skLineSegment(sketch, "E103.right", {"start": v(4934.69, -4699.04) * mm, "end": v(5384.69, -4699.04) * mm});
            skLineSegment(sketch, "E104.bottom", {"start": v(4917.88, -7746.4) * mm, "end": v(4917.88, -6246.4) * mm});
            skLineSegment(sketch, "E104.top", {"start": v(5367.88, -7746.4) * mm, "end": v(5367.88, -6246.4) * mm});
            skLineSegment(sketch, "E104.left", {"start": v(4917.88, -7746.4) * mm, "end": v(5367.88, -7746.4) * mm});
            skLineSegment(sketch, "E104.right", {"start": v(4917.88, -6246.4) * mm, "end": v(5367.88, -6246.4) * mm});
            skLineSegment(sketch, "E105.bottom", {"start": v(4917.88, -7856.4) * mm, "end": v(5817.88, -7856.4) * mm});
            skLineSegment(sketch, "E105.top", {"start": v(4917.88, -8456.4) * mm, "end": v(5817.88, -8456.4) * mm});
            skLineSegment(sketch, "E105.left", {"start": v(4917.88, -7856.4) * mm, "end": v(4917.88, -8456.4) * mm});
            skLineSegment(sketch, "E105.right", {"start": v(5817.88, -7856.4) * mm, "end": v(5817.88, -8456.4) * mm});
            skLineSegment(sketch, "E106.bottom", {"start": v(6717.4, -6639.62) * mm, "end": v(7517.4, -6639.62) * mm});
            skLineSegment(sketch, "E106.top", {"start": v(6717.4, -8139.62) * mm, "end": v(7517.4, -8139.62) * mm});
            skLineSegment(sketch, "E106.left", {"start": v(6717.4, -6639.62) * mm, "end": v(6717.4, -8139.62) * mm});
            skLineSegment(sketch, "E106.right", {"start": v(7517.4, -6639.62) * mm, "end": v(7517.4, -8139.62) * mm});
            skLineSegment(sketch, "E107.bottom", {"start": v(6717.4, -5064.93) * mm, "end": v(7517.4, -5064.93) * mm});
            skLineSegment(sketch, "E107.top", {"start": v(6717.4, -6564.93) * mm, "end": v(7517.4, -6564.93) * mm});
            skLineSegment(sketch, "E107.left", {"start": v(6717.4, -5064.93) * mm, "end": v(6717.4, -6564.93) * mm});
            skLineSegment(sketch, "E107.right", {"start": v(7517.4, -5064.93) * mm, "end": v(7517.4, -6564.93) * mm});
            skLineSegment(sketch, "E108.bottom", {"start": v(9371.63, -7992.01) * mm, "end": v(9371.63, -6492.01) * mm});
            skLineSegment(sketch, "E108.top", {"start": v(9821.63, -7992.01) * mm, "end": v(9821.63, -6492.01) * mm});
            skLineSegment(sketch, "E108.left", {"start": v(9371.63, -7992.01) * mm, "end": v(9821.63, -7992.01) * mm});
            skLineSegment(sketch, "E108.right", {"start": v(9371.63, -6492.01) * mm, "end": v(9821.63, -6492.01) * mm});
            skLineSegment(sketch, "E109.bottom", {"start": v(9394.44, -6459.68) * mm, "end": v(9394.44, -4959.68) * mm});
            skLineSegment(sketch, "E109.top", {"start": v(9844.44, -6459.68) * mm, "end": v(9844.44, -4959.68) * mm});
            skLineSegment(sketch, "E109.left", {"start": v(9394.44, -6459.68) * mm, "end": v(9844.44, -6459.68) * mm});
            skLineSegment(sketch, "E109.right", {"start": v(9394.44, -4959.68) * mm, "end": v(9844.44, -4959.68) * mm});
            skLineSegment(sketch, "E110.bottom", {"start": v(7557.4, -7389.62) * mm, "end": v(8307.4, -7389.62) * mm});
            skLineSegment(sketch, "E110.top", {"start": v(7557.4, -8139.62) * mm, "end": v(8307.4, -8139.62) * mm});
            skLineSegment(sketch, "E110.left", {"start": v(7557.4, -7389.62) * mm, "end": v(7557.4, -8139.62) * mm});
            skLineSegment(sketch, "E110.right", {"start": v(8307.4, -7389.62) * mm, "end": v(8307.4, -8139.62) * mm});
            skLineSegment(sketch, "E111.bottom", {"start": v(7557.4, -6612.02) * mm, "end": v(8307.4, -6612.02) * mm});
            skLineSegment(sketch, "E111.top", {"start": v(7557.4, -7362.02) * mm, "end": v(8307.4, -7362.02) * mm});
            skLineSegment(sketch, "E111.left", {"start": v(7557.4, -6612.02) * mm, "end": v(7557.4, -7362.02) * mm});
            skLineSegment(sketch, "E111.right", {"start": v(8307.4, -6612.02) * mm, "end": v(8307.4, -7362.02) * mm});
            skLineSegment(sketch, "E112.bottom", {"start": v(7567.14, -5064.93) * mm, "end": v(8367.14, -5064.93) * mm});
            skLineSegment(sketch, "E112.top", {"start": v(7567.14, -6564.93) * mm, "end": v(8367.14, -6564.93) * mm});
            skLineSegment(sketch, "E112.left", {"start": v(7567.14, -5064.93) * mm, "end": v(7567.14, -6564.93) * mm});
            skLineSegment(sketch, "E112.right", {"start": v(8367.14, -5064.93) * mm, "end": v(8367.14, -6564.93) * mm});
            skLineSegment(sketch, "E113.bottom", {"start": v(9168.03, -8059.64) * mm, "end": v(9868.03, -8059.64) * mm});
            skLineSegment(sketch, "E113.top", {"start": v(9168.03, -8459.64) * mm, "end": v(9868.03, -8459.64) * mm});
            skLineSegment(sketch, "E113.left", {"start": v(9168.03, -8059.64) * mm, "end": v(9168.03, -8459.64) * mm});
            skLineSegment(sketch, "E113.right", {"start": v(9868.03, -8059.64) * mm, "end": v(9868.03, -8459.64) * mm});
            skLineSegment(sketch, "E114.bottom", {"start": v(9821.63, -2103.18) * mm, "end": v(8321.63, -2103.18) * mm});
            skLineSegment(sketch, "E114.top", {"start": v(9821.63, -1653.18) * mm, "end": v(8321.63, -1653.18) * mm});
            skLineSegment(sketch, "E114.left", {"start": v(9821.63, -2103.18) * mm, "end": v(9821.63, -1653.18) * mm});
            skLineSegment(sketch, "E114.right", {"start": v(8321.63, -2103.18) * mm, "end": v(8321.63, -1653.18) * mm});
            skLineSegment(sketch, "E115.bottom", {"start": v(8217.4, -2103.18) * mm, "end": v(6717.4, -2103.18) * mm});
            skLineSegment(sketch, "E115.top", {"start": v(8217.4, -1653.18) * mm, "end": v(6717.4, -1653.18) * mm});
            skLineSegment(sketch, "E115.left", {"start": v(8217.4, -2103.18) * mm, "end": v(8217.4, -1653.18) * mm});
            skLineSegment(sketch, "E115.right", {"start": v(6717.4, -2103.18) * mm, "end": v(6717.4, -1653.18) * mm});
            skLineSegment(sketch, "E116.bottom", {"start": v(9821.63, -3144.82) * mm, "end": v(8321.63, -3144.82) * mm});
            skLineSegment(sketch, "E116.top", {"start": v(9821.63, -2694.82) * mm, "end": v(8321.63, -2694.82) * mm});
            skLineSegment(sketch, "E116.left", {"start": v(9821.63, -3144.82) * mm, "end": v(9821.63, -2694.82) * mm});
            skLineSegment(sketch, "E116.right", {"start": v(8321.63, -3144.82) * mm, "end": v(8321.63, -2694.82) * mm});
            skLineSegment(sketch, "E117.bottom", {"start": v(8217.4, -3144.82) * mm, "end": v(6717.4, -3144.82) * mm});
            skLineSegment(sketch, "E117.top", {"start": v(8217.4, -2694.82) * mm, "end": v(6717.4, -2694.82) * mm});
            skLineSegment(sketch, "E117.left", {"start": v(8217.4, -3144.82) * mm, "end": v(8217.4, -2694.82) * mm});
            skLineSegment(sketch, "E117.right", {"start": v(6717.4, -3144.82) * mm, "end": v(6717.4, -2694.82) * mm});
            skLineSegment(sketch, "E118.bottom", {"start": v(9867.14, -4182.91) * mm, "end": v(8367.14, -4182.91) * mm});
            skLineSegment(sketch, "E118.top", {"start": v(9867.14, -3732.91) * mm, "end": v(8367.14, -3732.91) * mm});
            skLineSegment(sketch, "E118.left", {"start": v(9867.14, -4182.91) * mm, "end": v(9867.14, -3732.91) * mm});
            skLineSegment(sketch, "E118.right", {"start": v(8367.14, -4182.91) * mm, "end": v(8367.14, -3732.91) * mm});
            skLineSegment(sketch, "E119.bottom", {"start": v(8217.4, -4182.4) * mm, "end": v(6717.4, -4182.4) * mm});
            skLineSegment(sketch, "E119.top", {"start": v(8217.4, -3732.4) * mm, "end": v(6717.4, -3732.4) * mm});
            skLineSegment(sketch, "E119.left", {"start": v(8217.4, -4182.4) * mm, "end": v(8217.4, -3732.4) * mm});
            skLineSegment(sketch, "E119.right", {"start": v(6717.4, -4182.4) * mm, "end": v(6717.4, -3732.4) * mm});
            skLineSegment(sketch, "E120.bottom", {"start": v(59.53, -4258.74) * mm, "end": v(759.53, -4258.74) * mm});
            skLineSegment(sketch, "E120.top", {"start": v(59.53, -4658.74) * mm, "end": v(759.53, -4658.74) * mm});
            skLineSegment(sketch, "E120.left", {"start": v(59.53, -4258.74) * mm, "end": v(59.53, -4658.74) * mm});
            skLineSegment(sketch, "E120.right", {"start": v(759.53, -4258.74) * mm, "end": v(759.53, -4658.74) * mm});
            skLineSegment(sketch, "E121.bottom", {"start": v(65, -2667.74) * mm, "end": v(865, -2667.74) * mm});
            skLineSegment(sketch, "E121.top", {"start": v(65, -4167.74) * mm, "end": v(865, -4167.74) * mm});
            skLineSegment(sketch, "E121.left", {"start": v(65, -2667.74) * mm, "end": v(65, -4167.74) * mm});
            skLineSegment(sketch, "E121.right", {"start": v(865, -2667.74) * mm, "end": v(865, -4167.74) * mm});
            skSolve(sketch);
        }
        {
            var Q0;
            Q0 = qSketchRegion(id + "F4", true);
            extrude(context, id + "F5", {"entities" : qUnion([Q0]), "operationType" : NewBodyOperationType.ADD, "depth" : 1 * mm});
        }
    });
